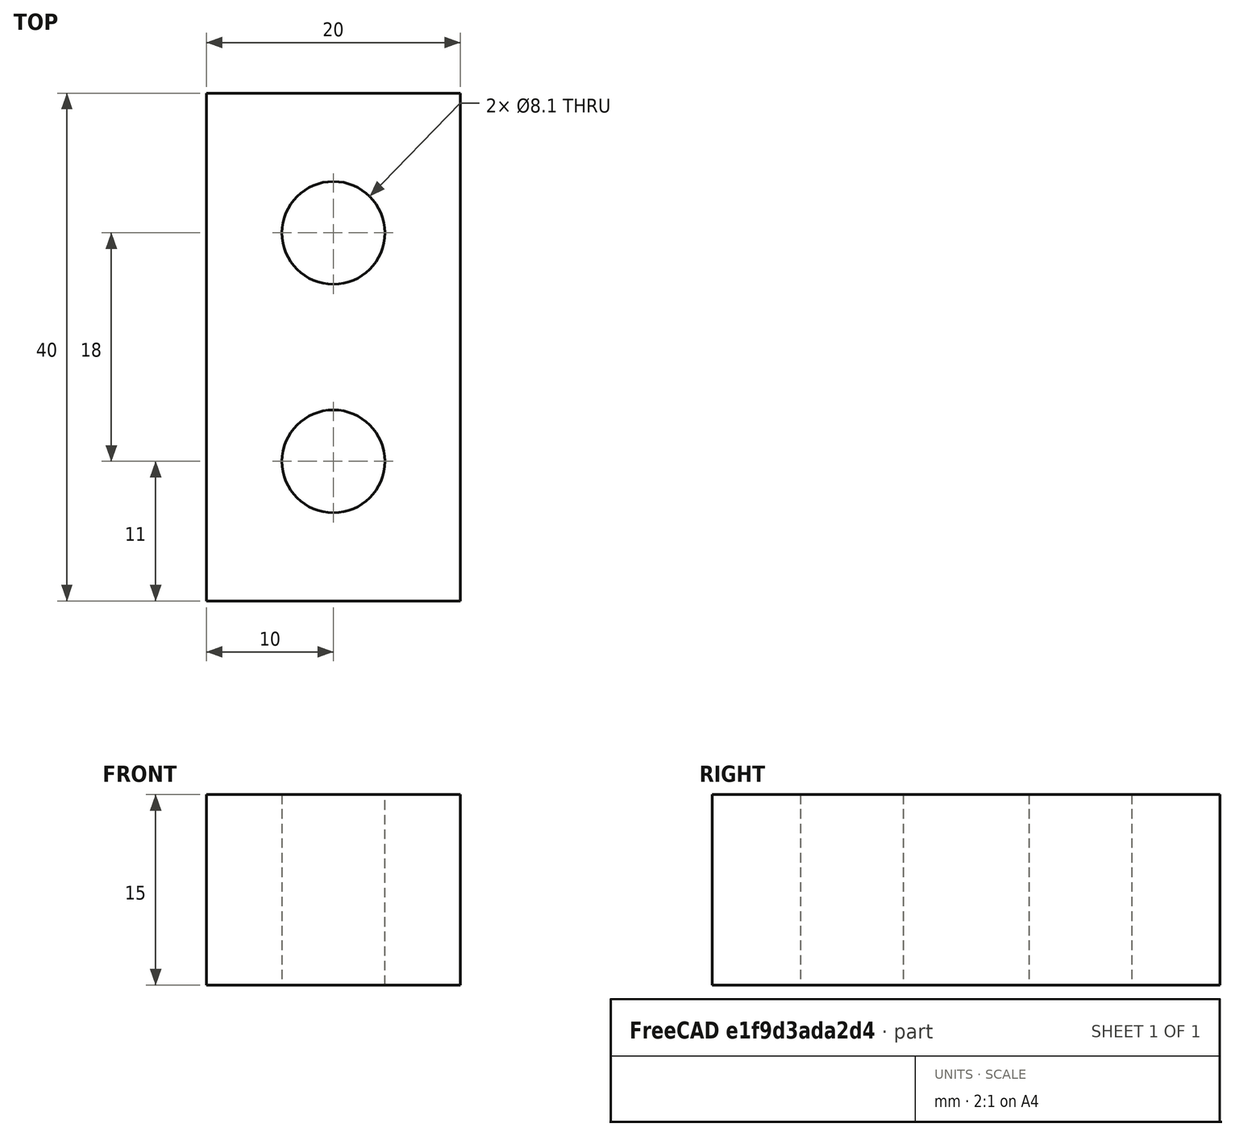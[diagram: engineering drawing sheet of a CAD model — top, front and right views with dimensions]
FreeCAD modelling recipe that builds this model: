
FCSTD DOCUMENT  (FreeCAD 0.21R33771 (Git))
Label: RodBlock
License: All rights reserved
LicenseURL: https://en.wikipedia.org/wiki/All_rights_reserved
objects: Sketcher::SketchObject×1, PartDesign::Pad×1, PartDesign::Body×1
note: 4 computed .brp shape members not serialized (recipe doc carries the construction recipe); baked Part::Feature solids carry a one-line shape summary decoded from their .brp

FEATURE [Sketcher::SketchObject] Sketch
  FullyConstrained = true
  MapMode = 5
  Support = -> [XY_Plane]
  sketch-geometry (7):
    g0: LineSegment StartX=-10 StartY=-20 StartZ=0 EndX=-10 EndY=20 EndZ=0
    g1: LineSegment StartX=-10 StartY=20 StartZ=0 EndX=10 EndY=20 EndZ=0
    g2: LineSegment StartX=10 StartY=20 StartZ=0 EndX=10 EndY=-20 EndZ=0
    g3: LineSegment StartX=10 StartY=-20 StartZ=0 EndX=-10 EndY=-20 EndZ=0
    g4: GeomPoint X=0 Y=0 Z=0
    g5: Circle CenterX=0 CenterY=9 CenterZ=0 NormalX=0 NormalY=0 NormalZ=1 AngleXU=0 Radius=4.05
    g6: Circle CenterX=0 CenterY=-9 CenterZ=0 NormalX=0 NormalY=0 NormalZ=1 AngleXU=0 Radius=4.05
  constraints (17):
    c: Coincident(g0,g1)
    c: Coincident(g1,g2)
    c: Coincident(g2,g3)
    c: Coincident(g3,g0)
    c: Horizontal(g1)
    c: Horizontal(g3)
    c: Vertical(g0)
    c: Vertical(g2)
    c: Symmetric(g1,g0,g4)
    c: Coincident(g4,g-1)
    c: DistanceX(g1,g1) = 20
    c: DistanceY(g2,g2) = 40
    c: Diameter(g5) = 8.1
    c: PointOnObject(g5,g-2)
    c: Equal(g5,g6) = 8.2
    c: DistanceY(g4,g5) = 9
    c: Symmetric(g5,g6,g-1)
FEATURE [PartDesign::Pad] Pad
  Direction = (0,0,1)
  Length = 15
  Length2 = 10
  Profile = -> Sketch
  ReferenceAxis = -> Sketch [N_Axis]
  Refine = true
  Type = 0
FEATURE [PartDesign::Body] Body
  Group = -> [Sketch,Pad]
  Origin = -> Origin
  Tip = -> Pad
